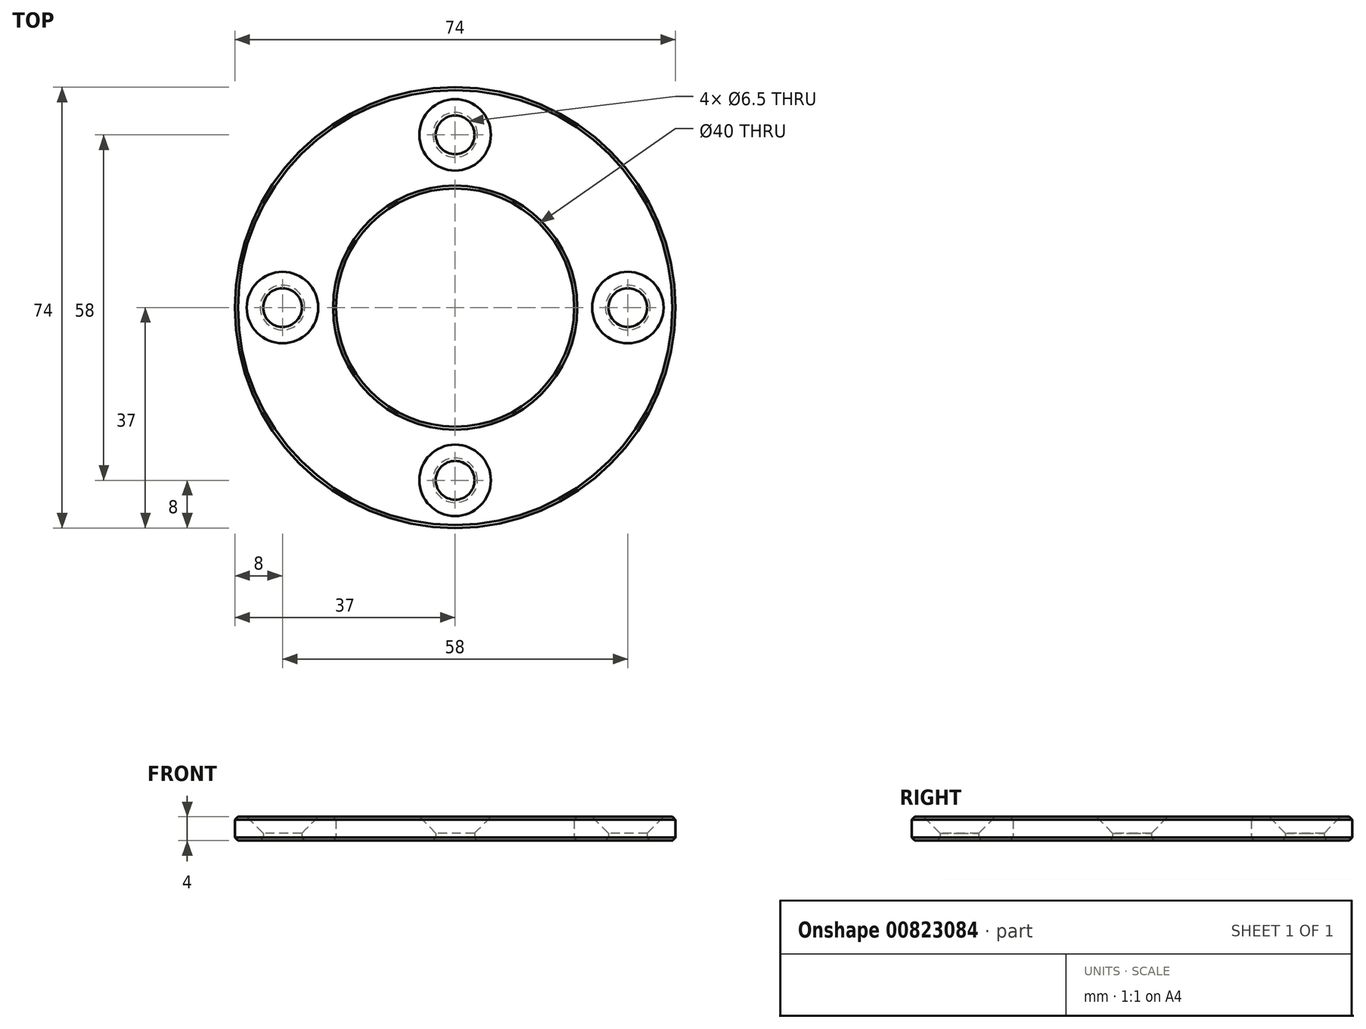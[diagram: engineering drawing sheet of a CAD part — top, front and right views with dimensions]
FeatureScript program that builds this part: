
annotation { "Feature Type Name" : "Feature", "Feature Type Description" : "" }
export const myFeature = defineFeature(function(context is Context, id is Id, definition is map)
    precondition{}
    {
        {
            var Q0;
            Q0=qCreatedBy(makeId("Top.planeOp"),FACE);
            var sketch = newSketch(context, id + "F0", { "sketchPlane" : qUnion([Q0])});
            skCircle(sketch, "E0", {"center": v(0, 0) * mm, "radius": 20 * mm});
            skCircle(sketch, "E1", {"center": v(0, 0) * mm, "radius": 29 * mm, "construction": true});
            skCircle(sketch, "E2", {"center": v(0, 0) * mm, "radius": 37 * mm});
            skLineSegment(sketch, "E3", {"start": v(0, -37) * mm, "end": v(0, 37) * mm, "construction": true});
            skLineSegment(sketch, "E4", {"start": v(0, 37) * mm, "end": v(37, 0) * mm, "construction": true});
            skLineSegment(sketch, "E5", {"start": v(37, 0) * mm, "end": v(-37, 0) * mm, "construction": true});
            skCircle(sketch, "E6", {"center": v(0, 29) * mm, "radius": 3.25 * mm});
            skCircle(sketch, "E7", {"center": v(-29, 0) * mm, "radius": 3.25 * mm});
            skCircle(sketch, "E8", {"center": v(0, -29) * mm, "radius": 3.25 * mm});
            skCircle(sketch, "E9", {"center": v(29, 0) * mm, "radius": 3.25 * mm});
            skSolve(sketch);
        }
        {
            var Q0;
            Q0 = qSketchRegion(id + "F0", true);
            extrude(context, id + "F1", {"entities" : qUnion([Q0]), "depth" : 4 * mm, "offsetDistance" : 25 * mm});
        }
        {
            var Q0;
            Q0=makeQuery(id+"F1.opExtrude","CAP_EDGE",EDGE,{"disambiguationData":[OSD([sQuery(id+"F0.wireOp",EDGE,"E8")])],"isStart":false});
            var Q1;
            Q1=makeQuery(id+"F1.opExtrude","CAP_EDGE",EDGE,{"disambiguationData":[OSD([sQuery(id+"F0.wireOp",EDGE,"E7")])],"isStart":false});
            var Q2;
            Q2=makeQuery(id+"F1.opExtrude","CAP_EDGE",EDGE,{"disambiguationData":[OSD([sQuery(id+"F0.wireOp",EDGE,"E6")])],"isStart":false});
            var Q3;
            Q3=makeQuery(id+"F1.opExtrude","CAP_EDGE",EDGE,{"disambiguationData":[OSD([sQuery(id+"F0.wireOp",EDGE,"E9")])],"isStart":false});
            chamfer(context, id + "F2", {"entities" : qUnion([Q0, Q1, Q2, Q3]), "width" : 2.75 * mm, "tangentPropagation" : true});
        }
        {
            var Q0;
            Q0=makeQuery(id+"F1.opExtrude","SWEPT_FACE",FACE,{"disambiguationData":[OSD([sQuery(id+"F0.wireOp",EDGE,"E0")])]});
            var Q1;
            Q1=makeQuery(id+"F1.opExtrude","SWEPT_FACE",FACE,{"disambiguationData":[OSD([sQuery(id+"F0.wireOp",EDGE,"E2")])]});
            var Q2;
            Q2=makeQuery(id+"F1.opExtrude","CAP_FACE",FACE,{"disambiguationData":[OSD([sQuery(id+"F0.wireOp",EDGE,"E0"),sQuery(id+"F0.wireOp",EDGE,"E2"),sQuery(id+"F0.wireOp",EDGE,"E6"),sQuery(id+"F0.wireOp",EDGE,"E7"),sQuery(id+"F0.wireOp",EDGE,"E8"),sQuery(id+"F0.wireOp",EDGE,"E9")])],"isStart":true});
            chamfer(context, id + "F3", {"entities" : qUnion([Q0, Q1, Q2]), "width" : 0.5 * mm, "tangentPropagation" : true});
        }
    });
